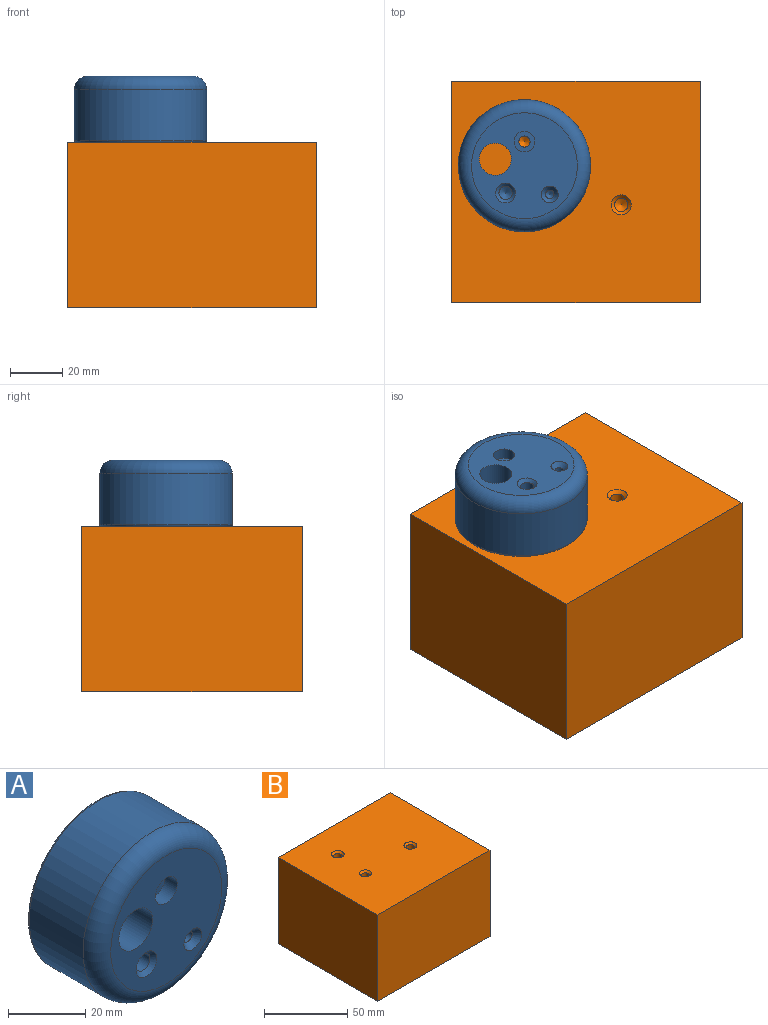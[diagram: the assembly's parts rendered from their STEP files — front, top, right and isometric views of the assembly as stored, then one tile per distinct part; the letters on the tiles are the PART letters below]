
ASSEMBLY  parts=2 mates=1
PART A: 15 faces, bbox 55x25.4x55 mm
  f0: cylinder r=25.4mm len=50.8mm, axis (0,1,0), area 3141.6mm2, adj f3,f10
  f1: plane 40.64x40.64mm, normal (0,-1,0), area 1049.2mm2, adj f3,f6,f9,f12,f14
  f2: plane 49.53x49.53mm, normal (0,1,0), area 1793.3mm2, adj f4,f10,f14
  f3: torus R=20.32mm, axis (0,-1,0), area 1180.9mm2, adj f0,f1
  f4: cylinder r=2.15mm len=21mm, axis (0,-1,0), area 283.7mm2, adj f2,f5
  f5: plane 8x8mm, normal (0,-1,0), area 35.7mm2, adj f4,f6
  f6: cylinder r=4mm len=8mm, axis (0,-1,0), area 110.6mm2, adj f1,f5
  f7: cone r=0mm half-angle=59deg, axis (0,-1,0), area 23.9mm2, adj f8
  f8: cylinder r=2.55mm len=17.36mm, axis (0,-1,0), area 278.4mm2, adj f7,f9
  f9: cone r=2.55mm half-angle=45deg, axis (0,-1,0), area 36mm2, adj f1,f8
  f10: torus R=24.77mm, axis (0,-1,0), area 157.7mm2, adj f0,f2
  f11: cylinder r=1.63mm len=14.87mm, axis (0,-1,0), area 152.5mm2, adj f12,f13
  f12: cone r=1.63mm half-angle=41deg, axis (0,-1,0), area 37.5mm2, adj f1,f11
  f13: cone r=0mm half-angle=59deg, axis (0,-1,0), area 9.8mm2, adj f11
  f14: cylinder r=6.15mm len=25.4mm, axis (0,-1,0), area 981.8mm2, adj f1,f2
PART B: 15 faces, bbox 95.4x84.8x63.5 mm
  f0: plane 95.44x63.5mm, normal (0,-1,0), area 6060.5mm2, adj f1,f3,f4,f5
  f1: plane 84.82x63.5mm, normal (1,0,0), area 5385.8mm2, adj f0,f2,f4,f5
  f2: plane 95.44x63.5mm, normal (0,1,0), area 6060.5mm2, adj f1,f3,f4,f5
  f3: plane 84.82x63.5mm, normal (-1,0,0), area 5385.8mm2, adj f0,f2,f4,f5
  f4: plane 95.44x84.82mm, normal (0,0,1), area 7962.8mm2, adj f0,f1,f2,f3,f12,f13,f14
  f5: plane 95.44x84.82mm, normal (0,0,-1), area 8094.9mm2, adj f0,f1,f2,f3
  f6: cone r=0mm half-angle=59deg, axis (0,0,1), area 23.9mm2, adj f7
  f7: cylinder r=2.55mm len=17.36mm, axis (0,0,1), area 278.4mm2, adj f6,f12
  f8: cone r=0mm half-angle=59deg, axis (0,0,1), area 23.9mm2, adj f9
  f9: cylinder r=2.55mm len=17.36mm, axis (0,0,1), area 278.4mm2, adj f8,f14
  f10: cone r=0mm half-angle=59deg, axis (0,0,1), area 19.6mm2, adj f11
  f11: cylinder r=2.31mm len=16.27mm, axis (0,0,1), area 236.3mm2, adj f10,f13
  f12: cone r=2.55mm half-angle=45deg, axis (0,0,1), area 36mm2, adj f4,f7
  f13: cone r=2.31mm half-angle=45deg, axis (0,0,1), area 33.2mm2, adj f4,f11
  f14: cone r=2.55mm half-angle=45deg, axis (0,0,1), area 36mm2, adj f4,f9
PLACE A rot(axis=(-1,0,0),90deg) t=(-19.79,9.99,63.5)mm
PLACE B at identity fixed
MATE planar A.f0 <-> B.f4  axis (0,0,-1) through (-19.79,9.99,63.5)mm
